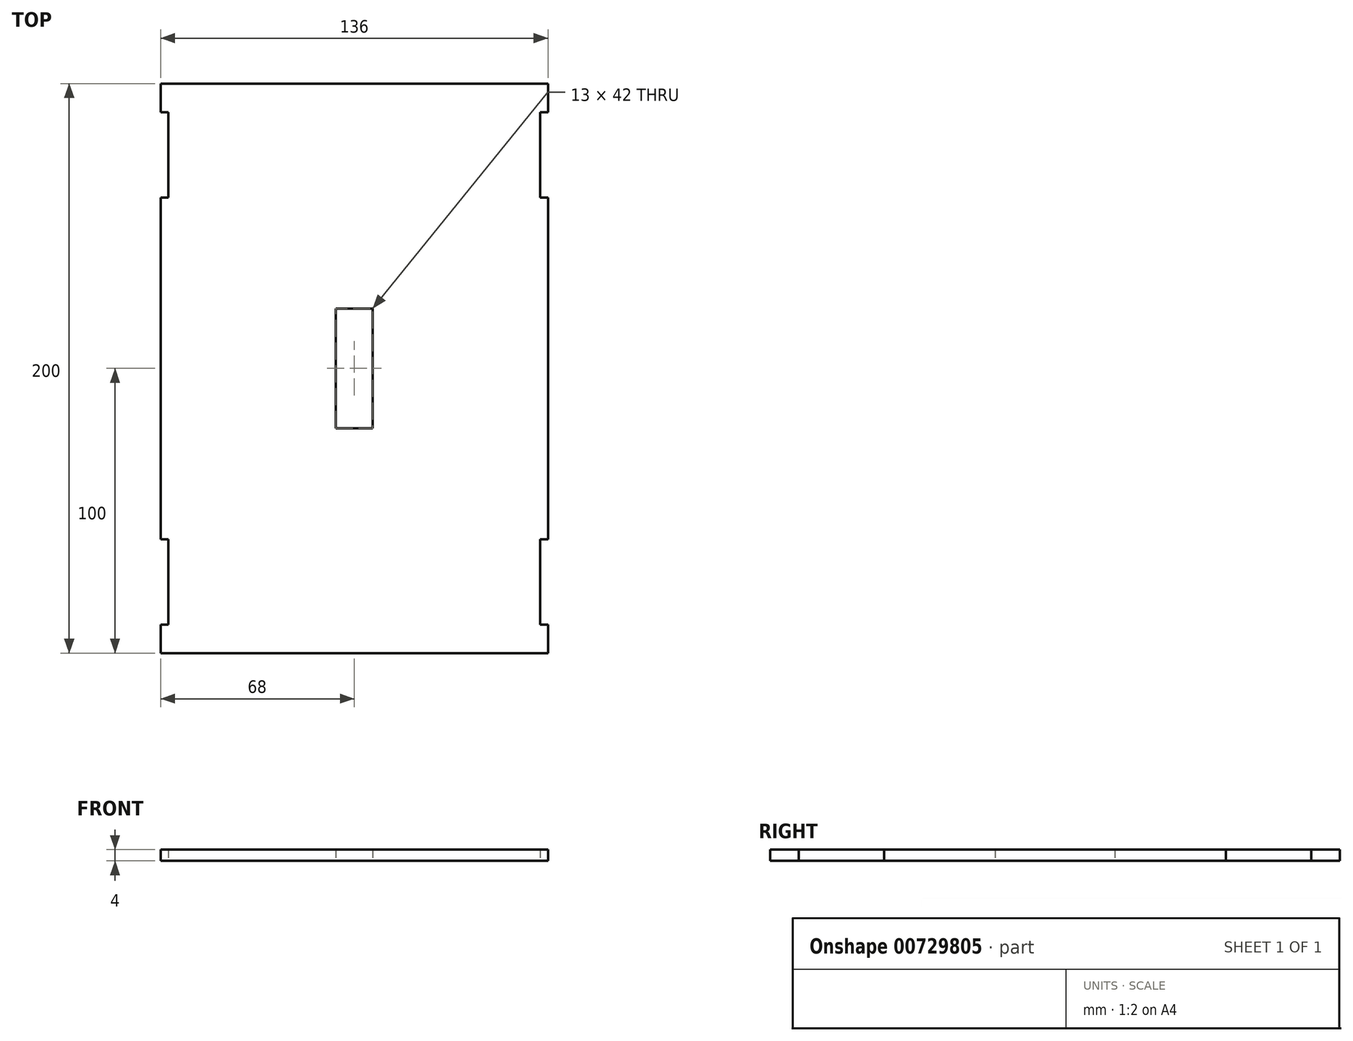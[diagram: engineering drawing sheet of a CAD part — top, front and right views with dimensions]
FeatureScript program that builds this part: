
annotation { "Feature Type Name" : "Feature", "Feature Type Description" : "" }
export const myFeature = defineFeature(function(context is Context, id is Id, definition is map)
    precondition{}
    {
        {
            var Q0;
            Q0=qCreatedBy(makeId("Top.planeOp"),FACE);
            var sketch = newSketch(context, id + "F0", { "sketchPlane" : qUnion([Q0])});
            skLineSegment(sketch, "E0.bottom", {"start": v(68, 100) * mm, "end": v(-68, 100) * mm});
            skLineSegment(sketch, "E0.top", {"start": v(68, -100) * mm, "end": v(-68, -100) * mm});
            skLineSegment(sketch, "E0.left", {"start": v(68, 100) * mm, "end": v(68, 90) * mm});
            skLineSegment(sketch, "E0.right", {"start": v(-68, 100) * mm, "end": v(-68, 90) * mm});
            skPoint(sketch, "E0.middle", {"position": v(0, 0) * mm});
            skLineSegment(sketch, "E1", {"start": v(68, -90) * mm, "end": v(65.3, -90) * mm});
            skLineSegment(sketch, "E2", {"start": v(65.3, -90) * mm, "end": v(65.3, -60) * mm});
            skLineSegment(sketch, "E3", {"start": v(65.3, -60) * mm, "end": v(68, -60) * mm});
            skLineSegment(sketch, "E4", {"start": v(68, 60) * mm, "end": v(65.3, 60) * mm});
            skLineSegment(sketch, "E5", {"start": v(65.3, 60) * mm, "end": v(65.3, 90) * mm});
            skLineSegment(sketch, "E6", {"start": v(65.3, 90) * mm, "end": v(68, 90) * mm});
            skLineSegment(sketch, "E7", {"start": v(-68, 90) * mm, "end": v(-65.3, 90) * mm});
            skLineSegment(sketch, "E8", {"start": v(-65.3, 90) * mm, "end": v(-65.3, 60) * mm});
            skLineSegment(sketch, "E9", {"start": v(-65.3, 60) * mm, "end": v(-68, 60) * mm});
            skLineSegment(sketch, "E10", {"start": v(-68, -60) * mm, "end": v(-65.3, -60) * mm});
            skLineSegment(sketch, "E11", {"start": v(-65.3, -60) * mm, "end": v(-65.3, -90) * mm});
            skLineSegment(sketch, "E12", {"start": v(-65.3, -90) * mm, "end": v(-68, -90) * mm});
            skLineSegment(sketch, "E13.trimOffspring", {"start": v(-68, 60) * mm, "end": v(-68, -60) * mm});
            skLineSegment(sketch, "E14.trimOffspring", {"start": v(-68, -90) * mm, "end": v(-68, -100) * mm});
            skLineSegment(sketch, "E15.trimOffspring", {"start": v(68, 60) * mm, "end": v(68, -60) * mm});
            skLineSegment(sketch, "E16.trimOffspring", {"start": v(68, -90) * mm, "end": v(68, -100) * mm});
            skLineSegment(sketch, "E17.bottom", {"start": v(-6.5, -21) * mm, "end": v(6.5, -21) * mm});
            skLineSegment(sketch, "E17.top", {"start": v(-6.5, 21) * mm, "end": v(6.5, 21) * mm});
            skLineSegment(sketch, "E17.left", {"start": v(-6.5, -21) * mm, "end": v(-6.5, 21) * mm});
            skLineSegment(sketch, "E17.right", {"start": v(6.5, -21) * mm, "end": v(6.5, 21) * mm});
            skSolve(sketch);
        }
        {
            var Q0;
            Q0 = qSketchRegion(id + "F0", true);
            extrude(context, id + "F1", {"entities" : qUnion([Q0]), "depth" : 4 * mm, "offsetDistance" : 25 * mm});
        }
    });
